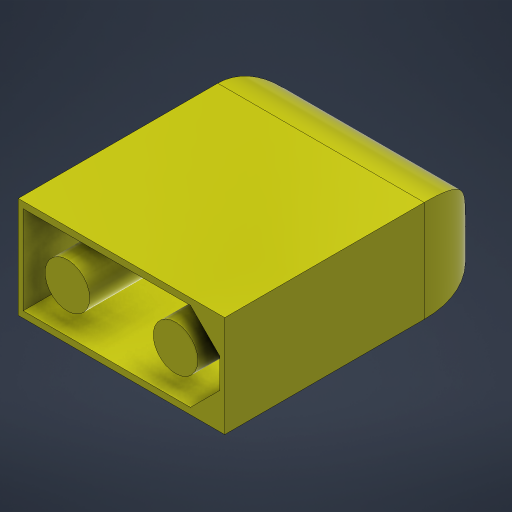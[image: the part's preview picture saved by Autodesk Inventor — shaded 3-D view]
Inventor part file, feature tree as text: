
AUTODESK INVENTOR PART (.ipt)
format: ipt  version: 2023.5 (Build 275446000, 446)  size: 238,080 bytes
history: native  units: mm
features: extrude x3, sketch x2, fillet x1, chamfer x1
ambient origin geometry x8: Origin, YZ Plane, XZ Plane, XY Plane, X Axis, Y Axis, Z Axis, Center Point
bodies: Volumenkörper1 (feature_tree)
feature tree (7):
  sketch  "Skizze1"  dims[d0=27.1mm d1=20.8mm]
  extrude  "Extrusion1"  Depth=20.8mm
  extrude  "Extrusion2"  Depth=10.0mm
  fillet  "Rundung1"  Radius=3.9mm
  chamfer  "Fase1"  Distance=10.9mm
  extrude  "Extrusion3"  Depth=11.0mm
  sketch  "Skizze2"  dims[d2=7.0mm d3=10.0mm d4=3.9mm d5=10.9mm d6=5.45mm d7=26.35mm d8=10.2mm d9=0.0mm d10=3.0mm d11=0.0mm d12=7.0mm d13=0.5mm d14=2.0mm d15=45.0deg d16=19.8mm d17=8.9mm d18=0.5mm d19=3.0mm d20=45.0deg d21=5.7mm d22=4.5mm d23=10.9mm d24=5.45mm d25=11.0mm d26=0.0mm]
